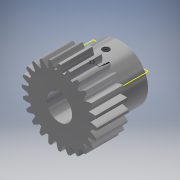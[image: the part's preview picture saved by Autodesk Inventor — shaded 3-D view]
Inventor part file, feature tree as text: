
AUTODESK INVENTOR PART (.ipt)
format: ipt  version: 2019 (Build 230136000, 136)  size: 290,304 bytes
history: native  units: mm (DEFAULTED — no unit token found)
features: sketch x6, plane x4, extrude x3, other x3, projected_geometry x2, hole x1
ambient origin geometry x8: Origin, YZ Plane, XZ Plane, XY Plane, X Axis, Y Axis, Z Axis, Center Point
bodies: Solid1 (feature_tree)
feature tree (19):
  extrude  "Extrusion1"  Depth=15.0mm TaperAngle=0.0deg
  plane  "Work Plane2"
  plane  "Work Plane8"
  plane  "Work Plane9"
  other  "正齒輪"
  extrude  "擠出2"  Depth=10.0mm TaperAngle=0.0deg
  extrude  "擠出3"  Depth=14.0mm
  sketch  "草圖5"
  plane  "工作平面11"
  hole  "孔1"  [1 undecoded]
  sketch  "Sketch1"  dims[d0=35.714032mm d1=15.0mm d2=0.0mm]
  sketch  "Sketch2"  dims[d3=33.355289mm d4=10.0mm d5=0.0mm d16=43.083915mm d17=0.0mm d34=1.308997mm d39=0.0mm d41=0.0mm d43=43.083915mm d46=43.083915mm d47=0.0mm d48=0.0mm d49=12.0mm d50=29.0mm d51=0.0mm d52=4.0mm d53=1.3mm d55=26.0mm d56=14.0mm d57=0.0mm d58=3.3mm d59=3.242mm d60=8.0mm d61=4.0mm d62=2.0mm d63=90.0deg d64=11.8mm d65=20.594885mm d66=0.75mm d67=20.594885mm d68=0.0625mm d69=0.75mm d70=0.375mm]
  other  "Srf1"
  sketch  "草圖3"
  sketch  "草圖4"
  projected_geometry  "投影迴路1"
  projected_geometry  "投影迴路2"
  sketch  "草圖6"
  other  "節圓直徑"
note: 1 required parameter value undecoded (feature->parameter linkage not recoverable at this tier; creation-order binding heuristic only, values carry confidence <= 0.55)
